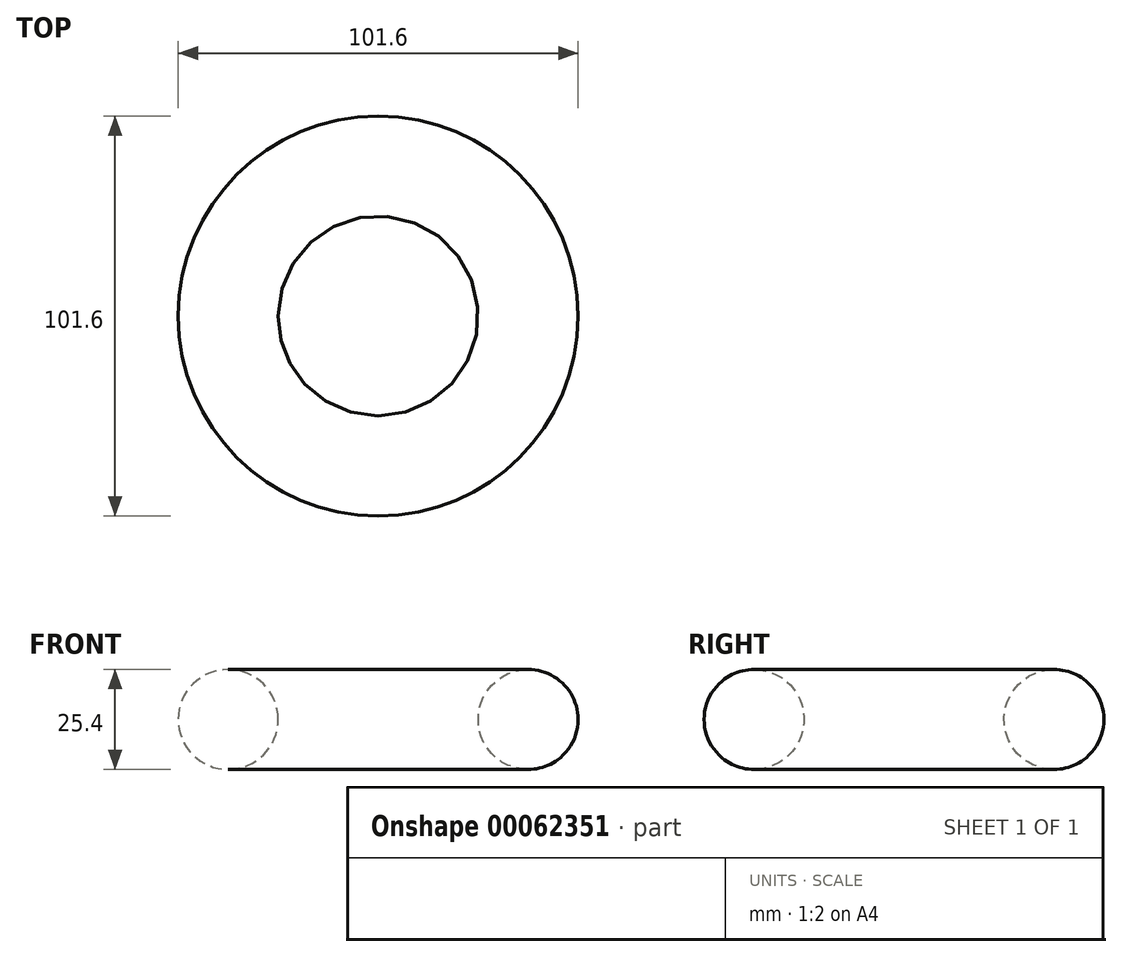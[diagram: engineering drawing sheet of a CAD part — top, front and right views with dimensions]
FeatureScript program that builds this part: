
annotation { "Feature Type Name" : "Feature", "Feature Type Description" : "" }
export const myFeature = defineFeature(function(context is Context, id is Id, definition is map)
    precondition{}
    {
        {
            var Q0;
            Q0=qCreatedBy(makeId("Front.planeOp"),FACE);
            var sketch = newSketch(context, id + "F0", { "sketchPlane" : qUnion([Q0])});
            skCircle(sketch, "E0", {"center": v(-38.1, 0) * mm, "radius": 12.7 * mm});
            skLineSegment(sketch, "E1", {"start": v(0, 0) * mm, "end": v(0, 42.68) * mm});
            skSolve(sketch);
        }
        {
            var Q0;
            Q0 = qSketchRegion(id + "F0", true);
            var Q1;
            Q1=sQuery(id+"F0.wireOp",EDGE,"E1");
            revolve(context, id + "F1", {"entities" : qUnion([Q0]), "axis" : qUnion([Q1]), "revolveType" : RevolveType.FULL});
        }
    });
